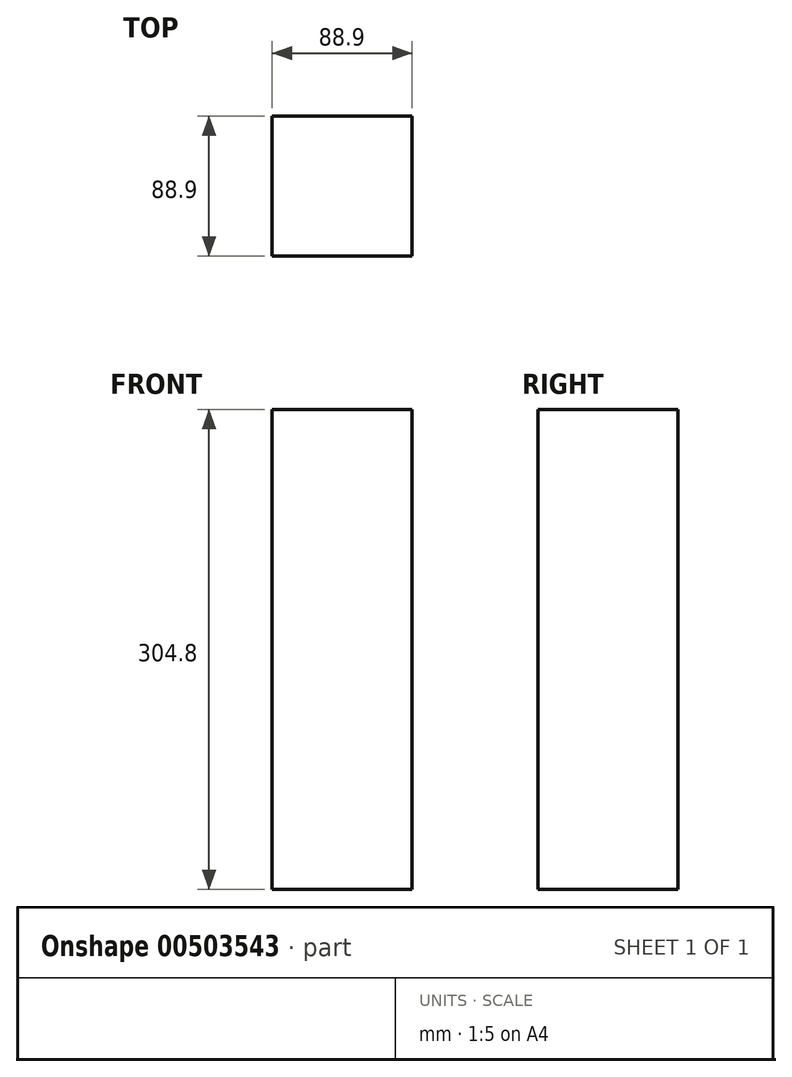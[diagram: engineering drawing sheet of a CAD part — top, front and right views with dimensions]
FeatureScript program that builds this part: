
annotation { "Feature Type Name" : "Feature", "Feature Type Description" : "" }
export const myFeature = defineFeature(function(context is Context, id is Id, definition is map)
    precondition{}
    {
        {
            var Q0;
            Q0=qCreatedBy(makeId("Top.planeOp"),FACE);
            var sketch = newSketch(context, id + "F0", { "sketchPlane" : qUnion([Q0])});
            skLineSegment(sketch, "E0.bottom", {"start": v(-44.45, 44.45) * mm, "end": v(44.45, 44.45) * mm});
            skLineSegment(sketch, "E0.top", {"start": v(-44.45, -44.45) * mm, "end": v(44.45, -44.45) * mm});
            skLineSegment(sketch, "E0.left", {"start": v(-44.45, 44.45) * mm, "end": v(-44.45, -44.45) * mm});
            skLineSegment(sketch, "E0.right", {"start": v(44.45, 44.45) * mm, "end": v(44.45, -44.45) * mm});
            skLineSegment(sketch, "E1", {"start": v(0, 81.79) * mm, "end": v(0, -72.9) * mm, "construction": true});
            skLineSegment(sketch, "E2", {"start": v(-83.57, 0) * mm, "end": v(82.23, 0) * mm, "construction": true});
            skSolve(sketch);
        }
        {
            var Q0;
            Q0=makeQuery(id+"F0.imprint","IMPRINT",FACE,{"disambiguationData":[TD([[makeQuery(id+"F0.imprint","IMPRINT",EDGE,{"derivedFrom":sQuery(id+"F0.wireOp",EDGE,"E0.bottom")}),-1.0]])]});
            extrude(context, id + "F1", {"entities" : qUnion([Q0]), "endBound" : BoundingType.SYMMETRIC, "depth" : 304.8 * mm});
        }
    });
